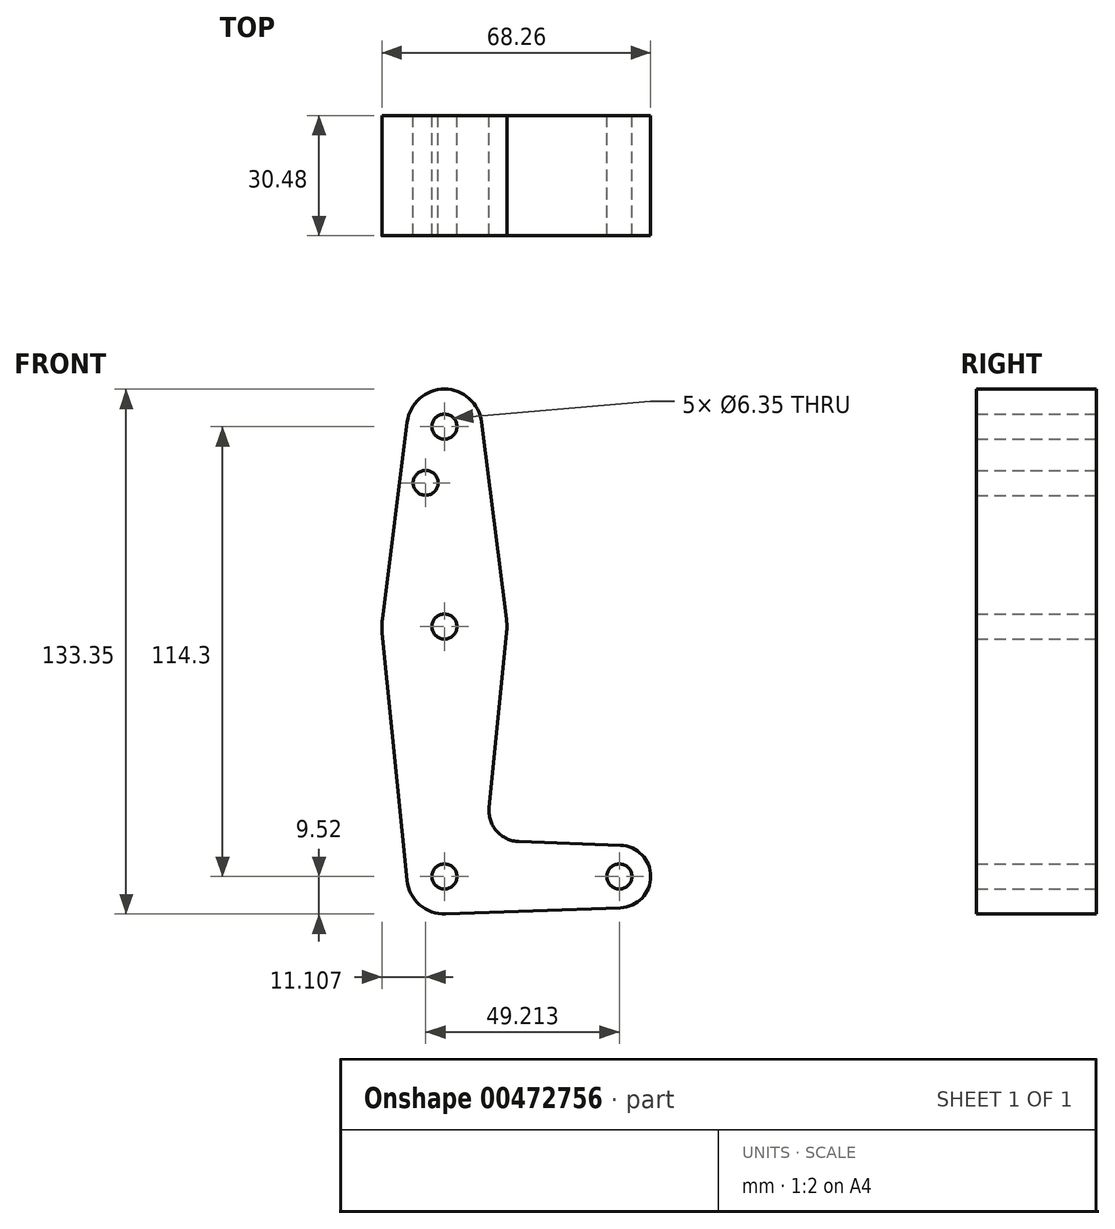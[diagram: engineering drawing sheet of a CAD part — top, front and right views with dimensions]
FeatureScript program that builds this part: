
annotation { "Feature Type Name" : "Feature", "Feature Type Description" : "" }
export const myFeature = defineFeature(function(context is Context, id is Id, definition is map)
    precondition{}
    {
        {
            var Q0;
            Q0=qCreatedBy(makeId("Front.planeOp"),FACE);
            var sketch = newSketch(context, id + "F0", { "sketchPlane" : qUnion([Q0])});
            skLineSegment(sketch, "E0", {"start": v(0, 0) * mm, "end": v(0, 63.5) * mm, "construction": true});
            skLineSegment(sketch, "E1", {"start": v(0, 63.5) * mm, "end": v(0, 114.3) * mm, "construction": true});
            skCircle(sketch, "E2", {"center": v(0, 114.3) * mm, "radius": 9.53 * mm});
            skCircle(sketch, "E3", {"center": v(0, 63.5) * mm, "radius": 15.88 * mm});
            skCircle(sketch, "E4", {"center": v(0, 0) * mm, "radius": 9.53 * mm});
            skLineSegment(sketch, "E5", {"start": v(0, 0) * mm, "end": v(44.45, 0) * mm, "construction": true});
            skCircle(sketch, "E6", {"center": v(44.45, 0) * mm, "radius": 7.94 * mm});
            skLineSegment(sketch, "E7", {"start": v(-9.45, 115.5) * mm, "end": v(-15.75, 65.48) * mm});
            skLineSegment(sketch, "E8", {"start": v(9.45, 115.5) * mm, "end": v(15.75, 65.48) * mm});
            skLineSegment(sketch, "E9", {"start": v(-15.8, 61.91) * mm, "end": v(-9.48, -0.95) * mm});
            skLineSegment(sketch, "E10", {"start": v(15.8, 61.91) * mm, "end": v(11.34, 17.6) * mm});
            skLineSegment(sketch, "E11", {"start": v(18.97, 8.85) * mm, "end": v(44.73, 7.93) * mm});
            skLineSegment(sketch, "E12", {"start": v(0.34, -9.52) * mm, "end": v(44.73, -7.93) * mm});
            skCircle(sketch, "E13", {"center": v(0, 114.3) * mm, "radius": 3.18 * mm});
            skCircle(sketch, "E14", {"center": v(0, 63.5) * mm, "radius": 3.18 * mm});
            skCircle(sketch, "E15", {"center": v(0, 0) * mm, "radius": 3.18 * mm});
            skCircle(sketch, "E16", {"center": v(44.45, 0) * mm, "radius": 3.18 * mm});
            skCircle(sketch, "E17", {"center": v(-4.76, 100.03) * mm, "radius": 3.18 * mm});
            skArc(sketch, "E18.filletArc", {"start": v(11.34, 17.6) * mm, "mid": v(13.26, 11.57) * mm, "end": v(18.97, 8.85) * mm});
            skSolve(sketch);
        }
        {
            var Q0;
            Q0 = qSketchRegion(id + "F0", true);
            extrude(context, id + "F1", {"entities" : qUnion([Q0]), "depth" : 30.48 * mm});
        }
    });
